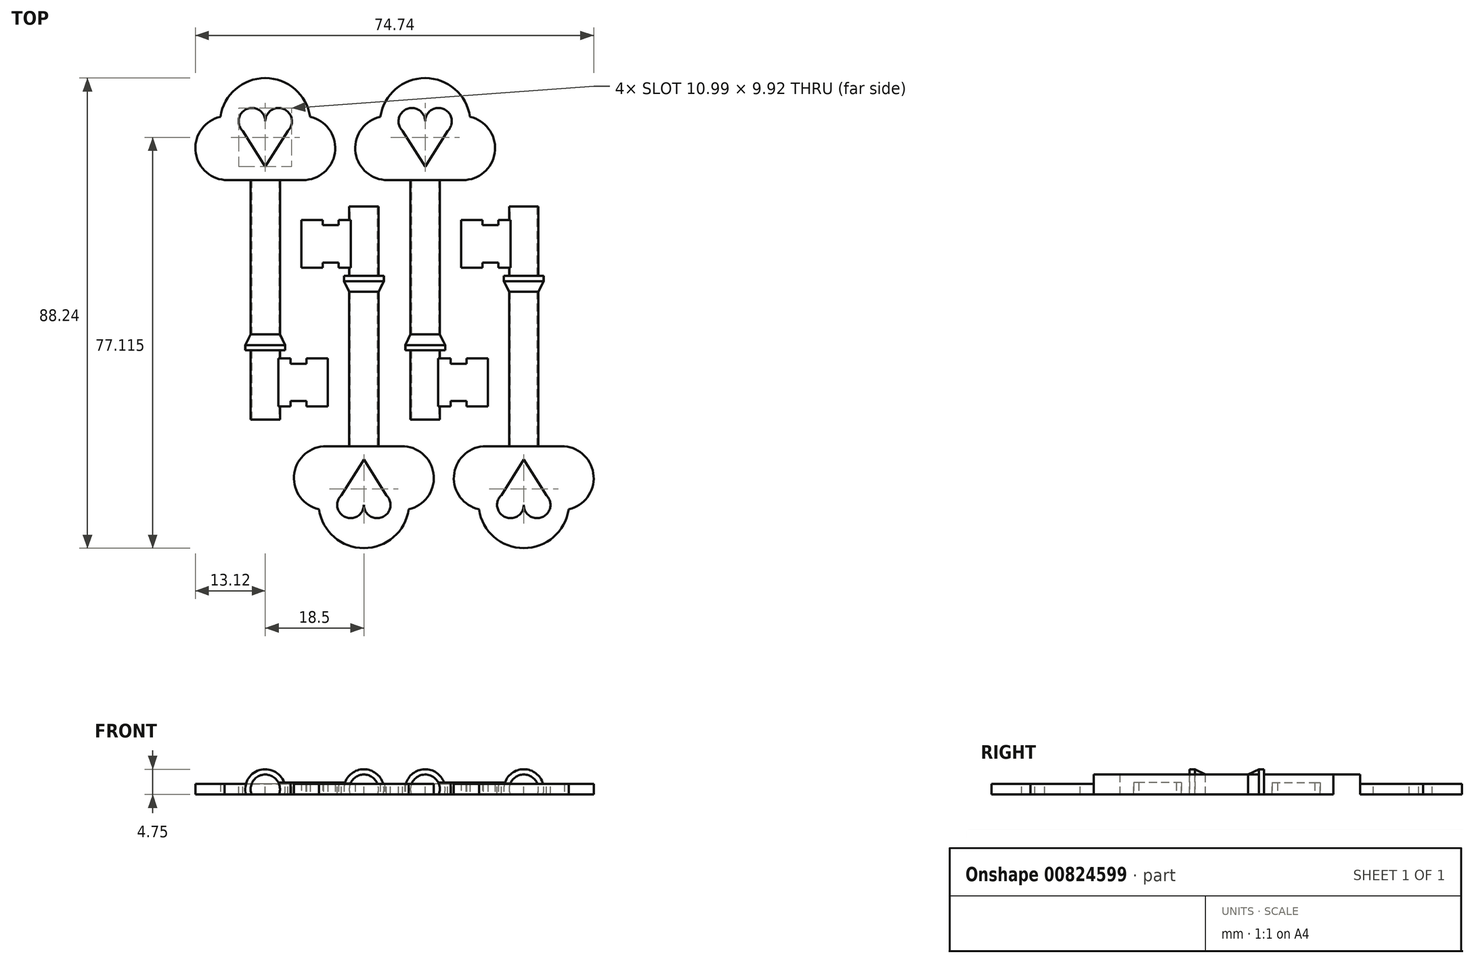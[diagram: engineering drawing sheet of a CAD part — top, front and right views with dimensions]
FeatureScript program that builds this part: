
annotation { "Feature Type Name" : "Feature", "Feature Type Description" : "" }
export const myFeature = defineFeature(function(context is Context, id is Id, definition is map)
    precondition{}
    {
        {
            var Q0;
            Q0=qCreatedBy(makeId("Top.planeOp"),FACE);
            var sketch = newSketch(context, id + "F0", { "sketchPlane" : qUnion([Q0])});
            skCircle(sketch, "E0", {"center": v(0, 35.62) * mm, "radius": 8.5 * mm});
            skCircle(sketch, "E1", {"center": v(-7.12, 30.98) * mm, "radius": 6 * mm});
            skCircle(sketch, "E2", {"center": v(7.12, 30.98) * mm, "radius": 6 * mm});
            skLineSegment(sketch, "E3", {"start": v(-7.62, 25) * mm, "end": v(7.62, 25) * mm});
            skLineSegment(sketch, "E4.bottom", {"start": v(-2.75, -20) * mm, "end": v(2.75, -20) * mm});
            skLineSegment(sketch, "E4.top", {"start": v(-2.75, 25) * mm, "end": v(2.75, 25) * mm});
            skLineSegment(sketch, "E4.left", {"start": v(-2.75, -20) * mm, "end": v(-2.75, 25) * mm});
            skLineSegment(sketch, "E4.right", {"start": v(2.75, -20) * mm, "end": v(2.75, 25) * mm});
            skLineSegment(sketch, "E5", {"start": v(0, 0) * mm, "end": v(0, -20) * mm, "construction": true});
            skLineSegment(sketch, "E6", {"start": v(0, 25) * mm, "end": v(0, 35.62) * mm, "construction": true});
            skLineSegment(sketch, "E7.bottom", {"start": v(2.75, -17.5) * mm, "end": v(11.75, -17.5) * mm});
            skLineSegment(sketch, "E7.top", {"start": v(2.75, -8.5) * mm, "end": v(11.75, -8.5) * mm});
            skLineSegment(sketch, "E7.left", {"start": v(2.75, -17.5) * mm, "end": v(2.75, -8.5) * mm});
            skLineSegment(sketch, "E7.right", {"start": v(11.75, -17.5) * mm, "end": v(11.75, -8.5) * mm});
            skLineSegment(sketch, "E8", {"start": v(11.75, -17.5) * mm, "end": v(7.75, -17.5) * mm});
            skLineSegment(sketch, "E9", {"start": v(7.75, -17.5) * mm, "end": v(7.75, -16.5) * mm});
            skLineSegment(sketch, "E10", {"start": v(7.75, -16.5) * mm, "end": v(4.75, -16.5) * mm});
            skLineSegment(sketch, "E11", {"start": v(4.75, -16.5) * mm, "end": v(4.75, -17.5) * mm});
            skLineSegment(sketch, "E12", {"start": v(11.75, -8.5) * mm, "end": v(7.75, -8.5) * mm});
            skLineSegment(sketch, "E13", {"start": v(7.75, -8.5) * mm, "end": v(7.75, -9.5) * mm});
            skLineSegment(sketch, "E14", {"start": v(7.75, -9.5) * mm, "end": v(4.75, -9.5) * mm});
            skLineSegment(sketch, "E15", {"start": v(4.75, -9.5) * mm, "end": v(4.75, -8.5) * mm});
            skLineSegment(sketch, "E16", {"start": v(0, -20) * mm, "end": v(0, 25) * mm});
            skLineSegment(sketch, "E17", {"start": v(2.75, -7) * mm, "end": v(3.75, -7) * mm});
            skLineSegment(sketch, "E18", {"start": v(3.75, -7) * mm, "end": v(3.75, -6) * mm});
            skLineSegment(sketch, "E19", {"start": v(3.75, -6) * mm, "end": v(2.75, -4) * mm});
            skLineSegment(sketch, "E20.bottom", {"start": v(2.75, -8.5) * mm, "end": v(0.83, -8.5) * mm});
            skLineSegment(sketch, "E20.top", {"start": v(2.75, -17.5) * mm, "end": v(0.83, -17.5) * mm});
            skLineSegment(sketch, "E20.left", {"start": v(2.75, -8.5) * mm, "end": v(2.75, -17.5) * mm});
            skLineSegment(sketch, "E20.right", {"start": v(0.83, -8.5) * mm, "end": v(0.83, -17.5) * mm});
            skCircle(sketch, "E21", {"center": v(0, 35.62) * mm, "radius": 5.15 * mm});
            skLineSegment(sketch, "E22", {"start": v(-5.06, 36.61) * mm, "end": v(5.06, 36.61) * mm});
            skSolve(sketch);
        }
        {
            var Q0;
            {var subQ3=sQuery(id+"F0.wireOp",EDGE,"E7.left");Q0=makeQuery(id+"F0.imprint","IMPRINT",FACE,{"disambiguationData":[TD([[makeQuery(id+"F0.imprint","IMPRINT",EDGE,{"derivedFrom":subQ3}),1.0]])]});}
            var Q1;
            {var subQ0=sQuery(id+"F0.wireOp",EDGE,"E17");Q1=makeQuery(id+"F0.imprint","IMPRINT",FACE,{"disambiguationData":[TD([[makeQuery(id+"F0.imprint","IMPRINT",EDGE,{"derivedFrom":subQ0}),1.0]])]});}
            var Q2;
            {var subQ7=sQuery(id+"F0.wireOp",EDGE,"E16");Q2=makeQuery(id+"F0.imprint","IMPRINT",FACE,{"disambiguationData":[TD([[makeQuery(id+"F0.imprint","IMPRINT",EDGE,{"derivedFrom":subQ7}),-1.0]])]});}
            var Q3;
            Q3=makeQuery(id+"F0.imprint","IMPRINT",FACE,{"disambiguationData":[TD([[makeQuery(id+"F0.imprint","IMPRINT",EDGE,{"derivedFrom":sQuery(id+"F0.wireOp",EDGE,"E20.bottom")}),1.0]])]});
            var Q4;
            Q4=sQuery(id+"F0.wireOp",EDGE,"E16");
            revolve(context, id + "F1", {"surfaceOperationType" : NewSurfaceOperationType.NEW, "entities" : qUnion([Q0, Q1, Q2, Q3]), "axis" : qUnion([Q4]), "revolveType" : RevolveType.FULL});
        }
        {
            var Q0;
            {var subQ3=sQuery(id+"F0.wireOp",EDGE,"E0");var subQ5=sQuery(id+"F0.wireOp",EDGE,"E1");var subQ9=makeQuery(id+"F0.imprint","INTERSECT",VERTEX,{"disambiguationData":[OD(1.0)],"derivedFrom":[subQ3,subQ5]});Q0=makeQuery(id+"F0.imprint","IMPRINT",FACE,{"disambiguationData":[TD([[makeQuery(id+"F0.imprint","IMPRINT",EDGE,{"disambiguationData":[TD([[subQ9,-1.0]])],"derivedFrom":subQ3}),-1.0]])]});}
            var Q1;
            {var subQ0=sQuery(id+"F0.wireOp",EDGE,"E1");var subQ1=sQuery(id+"F0.wireOp",EDGE,"E0");var subQ2=makeQuery(id+"F0.imprint","INTERSECT",VERTEX,{"disambiguationData":[OD(0.0)],"derivedFrom":[subQ1,subQ0]});Q1=makeQuery(id+"F0.imprint","IMPRINT",FACE,{"disambiguationData":[TD([[makeQuery(id+"F0.imprint","IMPRINT",EDGE,{"disambiguationData":[TD([[subQ2,1.0]])],"derivedFrom":subQ1}),1.0]])]});}
            var Q2;
            {var subQ0=sQuery(id+"F0.wireOp",EDGE,"E1");var subQ1=sQuery(id+"F0.wireOp",EDGE,"E0");var subQ2=makeQuery(id+"F0.imprint","INTERSECT",VERTEX,{"disambiguationData":[OD(0.0)],"derivedFrom":[subQ1,subQ0]});Q2=makeQuery(id+"F0.imprint","IMPRINT",FACE,{"disambiguationData":[TD([[makeQuery(id+"F0.imprint","IMPRINT",EDGE,{"disambiguationData":[TD([[subQ2,-1.0]])],"derivedFrom":subQ1}),1.0]])]});}
            var Q3;
            {var subQ0=sQuery(id+"F0.wireOp",EDGE,"E1");var subQ1=sQuery(id+"F0.wireOp",EDGE,"E0");var subQ2=makeQuery(id+"F0.imprint","INTERSECT",VERTEX,{"disambiguationData":[OD(0.0)],"derivedFrom":[subQ1,subQ0]});Q3=makeQuery(id+"F0.imprint","IMPRINT",FACE,{"disambiguationData":[TD([[makeQuery(id+"F0.imprint","IMPRINT",EDGE,{"disambiguationData":[TD([[subQ2,-1.0]])],"derivedFrom":subQ1}),-1.0]])]});}
            var Q4;
            {var subQ0=sQuery(id+"F0.wireOp",EDGE,"E2");var subQ1=sQuery(id+"F0.wireOp",EDGE,"E0");var subQ2=makeQuery(id+"F0.imprint","INTERSECT",VERTEX,{"disambiguationData":[OD(0.0)],"derivedFrom":[subQ1,subQ0]});Q4=makeQuery(id+"F0.imprint","IMPRINT",FACE,{"disambiguationData":[TD([[makeQuery(id+"F0.imprint","IMPRINT",EDGE,{"disambiguationData":[TD([[subQ2,1.0]])],"derivedFrom":subQ1}),-1.0]])]});}
            var Q5;
            {var subQ0=sQuery(id+"F0.wireOp",EDGE,"E2");var subQ1=sQuery(id+"F0.wireOp",EDGE,"E0");var subQ2=makeQuery(id+"F0.imprint","INTERSECT",VERTEX,{"disambiguationData":[OD(0.0)],"derivedFrom":[subQ1,subQ0]});Q5=makeQuery(id+"F0.imprint","IMPRINT",FACE,{"disambiguationData":[TD([[makeQuery(id+"F0.imprint","IMPRINT",EDGE,{"disambiguationData":[TD([[subQ2,1.0]])],"derivedFrom":subQ1}),1.0]])]});}
            var Q6;
            {var subQ0=sQuery(id+"F0.wireOp",EDGE,"E21");var subQ1=sQuery(id+"F0.wireOp",EDGE,"E1");var subQ3=makeQuery(id+"F0.imprint","INTERSECT",VERTEX,{"derivedFrom":[subQ1,subQ0]});Q6=makeQuery(id+"F0.imprint","IMPRINT",FACE,{"disambiguationData":[TD([[makeQuery(id+"F0.imprint","IMPRINT",EDGE,{"disambiguationData":[TD([[subQ3,-1.0]])],"derivedFrom":subQ1}),1.0]])]});}
            var Q7;
            {var subQ0=sQuery(id+"F0.wireOp",EDGE,"E22");Q7=makeQuery(id+"F0.imprint","IMPRINT",FACE,{"disambiguationData":[TD([[makeQuery(id+"F0.imprint","IMPRINT",EDGE,{"derivedFrom":subQ0}),-1.0]])]});}
            var Q8;
            {var subQ0=sQuery(id+"F0.wireOp",EDGE,"E21");var subQ1=sQuery(id+"F0.wireOp",EDGE,"E2");var subQ3=makeQuery(id+"F0.imprint","INTERSECT",VERTEX,{"derivedFrom":[subQ1,subQ0]});Q8=makeQuery(id+"F0.imprint","IMPRINT",FACE,{"disambiguationData":[TD([[makeQuery(id+"F0.imprint","IMPRINT",EDGE,{"disambiguationData":[TD([[subQ3,1.0]])],"derivedFrom":subQ1}),1.0]])]});}
            var Q9;
            {var subQ0=sQuery(id+"F0.wireOp",EDGE,"E1");var subQ1=sQuery(id+"F0.wireOp",EDGE,"E0");var subQ2=makeQuery(id+"F0.imprint","INTERSECT",VERTEX,{"disambiguationData":[OD(1.0)],"derivedFrom":[subQ1,subQ0]});Q9=makeQuery(id+"F0.imprint","IMPRINT",FACE,{"disambiguationData":[TD([[makeQuery(id+"F0.imprint","IMPRINT",EDGE,{"disambiguationData":[TD([[subQ2,-1.0]])],"derivedFrom":subQ1}),1.0]])]});}
            var Q10;
            {var subQ0=sQuery(id+"F0.wireOp",EDGE,"E22");Q10=makeQuery(id+"F0.imprint","IMPRINT",FACE,{"disambiguationData":[TD([[makeQuery(id+"F0.imprint","IMPRINT",EDGE,{"derivedFrom":subQ0}),1.0]])]});}
            extrude(context, id + "F2", {"entities" : qUnion([Q0, Q1, Q2, Q3, Q4, Q5, Q6, Q7, Q8, Q9, Q10]), "operationType" : NewBodyOperationType.ADD, "endBound" : BoundingType.SYMMETRIC, "depth" : 2 * mm, "offsetDistance" : 25 * mm});
        }
        {
            var Q0;
            Q0=makeQuery(id+"F0.imprint","IMPRINT",FACE,{"disambiguationData":[TD([[makeQuery(id+"F0.imprint","IMPRINT",EDGE,{"derivedFrom":sQuery(id+"F0.wireOp",EDGE,"E20.bottom")}),1.0]])]});
            var Q1;
            Q1=makeQuery(id+"F0.imprint","IMPRINT",FACE,{"disambiguationData":[TD([[makeQuery(id+"F0.imprint","IMPRINT",EDGE,{"derivedFrom":sQuery(id+"F0.wireOp",EDGE,"E7.right")}),1.0]])]});
            extrude(context, id + "F3", {"entities" : qUnion([Q0, Q1]), "operationType" : NewBodyOperationType.ADD, "endBound" : BoundingType.SYMMETRIC, "depth" : 2.5 * mm, "offsetDistance" : 25 * mm});
        }
        {
            var Q0;
            Q0=qCreatedBy(makeId("Top.planeOp"),FACE);
            var sketch = newSketch(context, id + "F4", { "sketchPlane" : qUnion([Q0])});
            skLineSegment(sketch, "E23.bottom", {"start": v(34.08, 51.7) * mm, "end": v(-26.71, 51.7) * mm});
            skLineSegment(sketch, "E23.top", {"start": v(34.08, -27.7) * mm, "end": v(-26.71, -27.7) * mm});
            skLineSegment(sketch, "E23.left", {"start": v(34.08, 51.7) * mm, "end": v(34.08, -27.7) * mm});
            skLineSegment(sketch, "E23.right", {"start": v(-26.71, 51.7) * mm, "end": v(-26.71, -27.7) * mm});
            skSolve(sketch);
        }
        {
            var Q0;
            Q0 = qSketchRegion(id + "F4", true);
            var Q1;
            Q1=makeQuery(id+"F2.opExtrude","CAP_FACE",FACE,{"disambiguationData":[OSD([sQuery(id+"F0.wireOp",EDGE,"E0"),sQuery(id+"F0.wireOp",EDGE,"E1"),sQuery(id+"F0.wireOp",EDGE,"E2"),sQuery(id+"F0.wireOp",EDGE,"E3"),sQuery(id+"F0.wireOp",EDGE,"E4.top"),sQuery(id+"F0.wireOp",EDGE,"E21"),sQuery(id+"F0.wireOp",EDGE,"E22")])],"isStart":true});
            extrude(context, id + "F5", {"entities" : qUnion([Q0]), "operationType" : NewBodyOperationType.REMOVE, "oppositeDirection" : true, "depth" : 5 * mm, "offsetDistance" : 25 * mm, "hasSecondDirection" : true, "secondDirectionBound" : SecondDirectionBoundingType.UP_TO_SURFACE, "secondDirectionOppositeDirection" : true, "secondDirectionDepth" : 1 * mm, "secondDirectionBoundEntityFace" : qUnion([Q1])});
        }
        {
            var Q0;
            Q0=makeQuery(id+"F2.opExtrude","CAP_FACE",FACE,{"disambiguationData":[OSD([sQuery(id+"F0.wireOp",EDGE,"E0"),sQuery(id+"F0.wireOp",EDGE,"E1"),sQuery(id+"F0.wireOp",EDGE,"E2"),sQuery(id+"F0.wireOp",EDGE,"E3"),sQuery(id+"F0.wireOp",EDGE,"E4.top")])],"isStart":false});
            var sketch = newSketch(context, id + "F6", { "sketchPlane" : qUnion([Q0])});
            skArc(sketch, "E24", {"start": v(0, 36) * mm, "mid": v(-3.49, 38.3) * mm, "end": v(-4.22, 34.19) * mm});
            skArc(sketch, "E25", {"start": v(4.22, 34.19) * mm, "mid": v(3.49, 38.3) * mm, "end": v(0, 36) * mm});
            skPoint(sketch, "E26", {"position": v(0, 36) * mm});
            skPoint(sketch, "E27", {"position": v(0, 25) * mm});
            skLineSegment(sketch, "E28", {"start": v(4.22, 34.19) * mm, "end": v(0, 27.5) * mm});
            skLineSegment(sketch, "E29", {"start": v(0, 27.5) * mm, "end": v(-4.22, 34.19) * mm});
            skSolve(sketch);
        }
        {
            var Q0;
            Q0=makeQuery(id+"F6.imprint","IMPRINT",FACE,{"disambiguationData":[TD([[makeQuery(id+"F6.imprint","IMPRINT",EDGE,{"derivedFrom":sQuery(id+"F6.wireOp",EDGE,"E24")}),1.0]])]});
            extrude(context, id + "F7", {"entities" : qUnion([Q0]), "operationType" : NewBodyOperationType.REMOVE, "oppositeDirection" : true, "depth" : 25 * mm, "offsetDistance" : 25 * mm});
        }
        {
            var Q0;
            Q0=makeQuery(id+"F1.opRevolve","SWEPT_BODY",BODY,{"disambiguationData":[OSD([sQuery(id+"F0.wireOp",EDGE,"E4.bottom"),sQuery(id+"F0.wireOp",EDGE,"E4.top"),sQuery(id+"F0.wireOp",EDGE,"E4.right"),sQuery(id+"F0.wireOp",EDGE,"E16"),sQuery(id+"F0.wireOp",EDGE,"E17"),sQuery(id+"F0.wireOp",EDGE,"E18"),sQuery(id+"F0.wireOp",EDGE,"E19"),sQuery(id+"F0.wireOp",EDGE,"E20.left")])]});
            transform(context, id + "F8", {"entities" : qUnion([Q0]), "transformType" : TransformType.TRANSLATION_3D, "dx" : 30 * mm, "dy" : 0 * mm, "dz" : 0 * mm, "makeCopy" : true});
        }
        {
            var Q0;
            Q0=makeQuery(id+"F8.opPattern","COPY",BODY,{"derivedFrom":makeQuery(id+"F1.opRevolve","SWEPT_BODY",BODY,{"disambiguationData":[OSD([sQuery(id+"F0.wireOp",EDGE,"E4.bottom"),sQuery(id+"F0.wireOp",EDGE,"E4.top"),sQuery(id+"F0.wireOp",EDGE,"E4.right"),sQuery(id+"F0.wireOp",EDGE,"E16"),sQuery(id+"F0.wireOp",EDGE,"E17"),sQuery(id+"F0.wireOp",EDGE,"E18"),sQuery(id+"F0.wireOp",EDGE,"E19"),sQuery(id+"F0.wireOp",EDGE,"E20.left")])]}),"instanceName":"1"});
            var Q1;
            Q1=makeQuery(id+"F8.opPattern","COPY",EDGE,{"derivedFrom":makeQuery(id+"F3.opExtrude","SWEPT_EDGE",EDGE,{"disambiguationData":[OSD([sQuery(id+"F0.wireOp",EDGE,"E7.bottom"),sQuery(id+"F0.wireOp",EDGE,"E8"),sQuery(id+"F0.wireOp",EDGE,"E9")])]}),"instanceName":"1"});
            transform(context, id + "F9", {"entities" : qUnion([Q0]), "transformType" : TransformType.ROTATION, "transformAxis" : qUnion([Q1]), "angle" : 180 * degree, "makeCopy" : false});
        }
        {
            var Q0;
            Q0=makeQuery(id+"F8.opPattern","COPY",BODY,{"derivedFrom":makeQuery(id+"F1.opRevolve","SWEPT_BODY",BODY,{"disambiguationData":[OSD([sQuery(id+"F0.wireOp",EDGE,"E4.bottom"),sQuery(id+"F0.wireOp",EDGE,"E4.top"),sQuery(id+"F0.wireOp",EDGE,"E4.right"),sQuery(id+"F0.wireOp",EDGE,"E16"),sQuery(id+"F0.wireOp",EDGE,"E17"),sQuery(id+"F0.wireOp",EDGE,"E18"),sQuery(id+"F0.wireOp",EDGE,"E19"),sQuery(id+"F0.wireOp",EDGE,"E20.left")])]}),"instanceName":"1"});
            transform(context, id + "F10", {"entities" : qUnion([Q0]), "transformType" : TransformType.TRANSLATION_3D, "dx" : -27 * mm, "dy" : 35 * mm, "dz" : 0 * mm, "makeCopy" : false});
        }
        {
            var Q0;
            Q0=makeQuery(id+"F1.opRevolve","SWEPT_BODY",BODY,{"disambiguationData":[OSD([sQuery(id+"F0.wireOp",EDGE,"E4.bottom"),sQuery(id+"F0.wireOp",EDGE,"E4.top"),sQuery(id+"F0.wireOp",EDGE,"E4.right"),sQuery(id+"F0.wireOp",EDGE,"E16"),sQuery(id+"F0.wireOp",EDGE,"E17"),sQuery(id+"F0.wireOp",EDGE,"E18"),sQuery(id+"F0.wireOp",EDGE,"E19"),sQuery(id+"F0.wireOp",EDGE,"E20.left")])]});
            var Q1;
            Q1=makeQuery(id+"F8.opPattern","COPY",BODY,{"derivedFrom":makeQuery(id+"F1.opRevolve","SWEPT_BODY",BODY,{"disambiguationData":[OSD([sQuery(id+"F0.wireOp",EDGE,"E4.bottom"),sQuery(id+"F0.wireOp",EDGE,"E4.top"),sQuery(id+"F0.wireOp",EDGE,"E4.right"),sQuery(id+"F0.wireOp",EDGE,"E16"),sQuery(id+"F0.wireOp",EDGE,"E17"),sQuery(id+"F0.wireOp",EDGE,"E18"),sQuery(id+"F0.wireOp",EDGE,"E19"),sQuery(id+"F0.wireOp",EDGE,"E20.left")])]}),"instanceName":"1"});
            transform(context, id + "F11", {"entities" : qUnion([Q0, Q1]), "transformType" : TransformType.TRANSLATION_3D, "dx" : -30 * mm, "dy" : 0 * mm, "dz" : 0 * mm, "makeCopy" : true});
        }
    });
